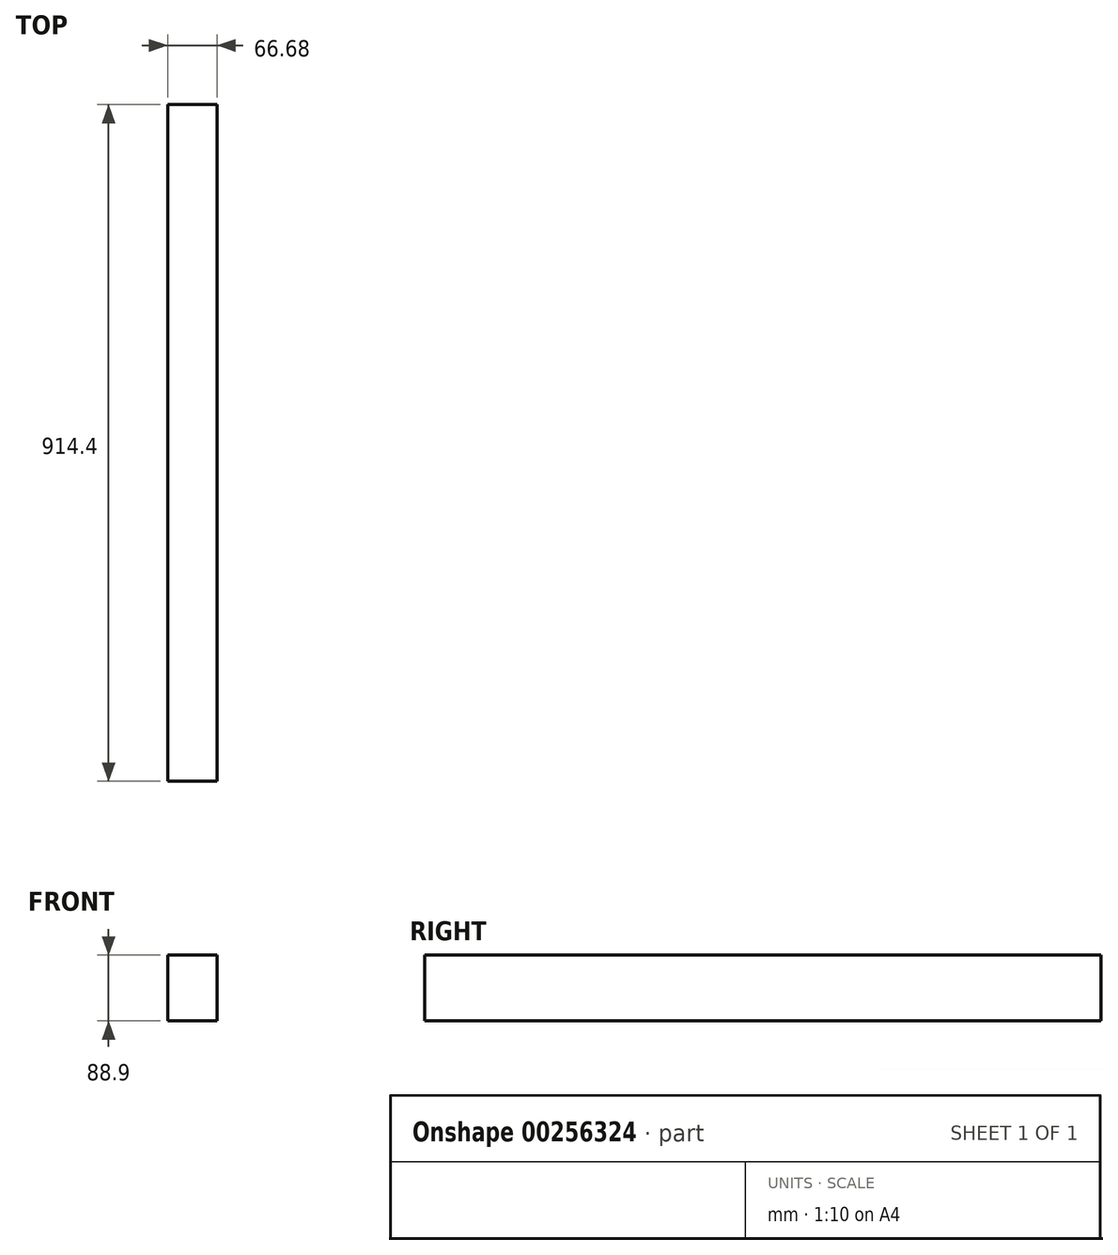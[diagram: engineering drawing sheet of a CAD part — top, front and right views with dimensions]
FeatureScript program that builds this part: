
annotation { "Feature Type Name" : "Feature", "Feature Type Description" : "" }
export const myFeature = defineFeature(function(context is Context, id is Id, definition is map)
    precondition{}
    {
        {
            var Q0;
            Q0=qCreatedBy(makeId("Front.planeOp"),FACE);
            var sketch = newSketch(context, id + "F0", { "sketchPlane" : qUnion([Q0])});
            skLineSegment(sketch, "E0.bottom", {"start": v(-33.34, 44.45) * mm, "end": v(33.34, 44.45) * mm});
            skLineSegment(sketch, "E0.top", {"start": v(-33.34, -44.45) * mm, "end": v(33.34, -44.45) * mm});
            skLineSegment(sketch, "E0.left", {"start": v(-33.34, 44.45) * mm, "end": v(-33.34, -44.45) * mm});
            skLineSegment(sketch, "E0.right", {"start": v(33.34, 44.45) * mm, "end": v(33.34, -44.45) * mm});
            skSolve(sketch);
        }
        {
            var Q0;
            Q0=qSketchRegion(id+"F0",true);
            extrude(context, id + "F1", {"entities" : qUnion([Q0]), "endBound" : BoundingType.SYMMETRIC, "depth" : 914.4 * mm});
        }
    });
